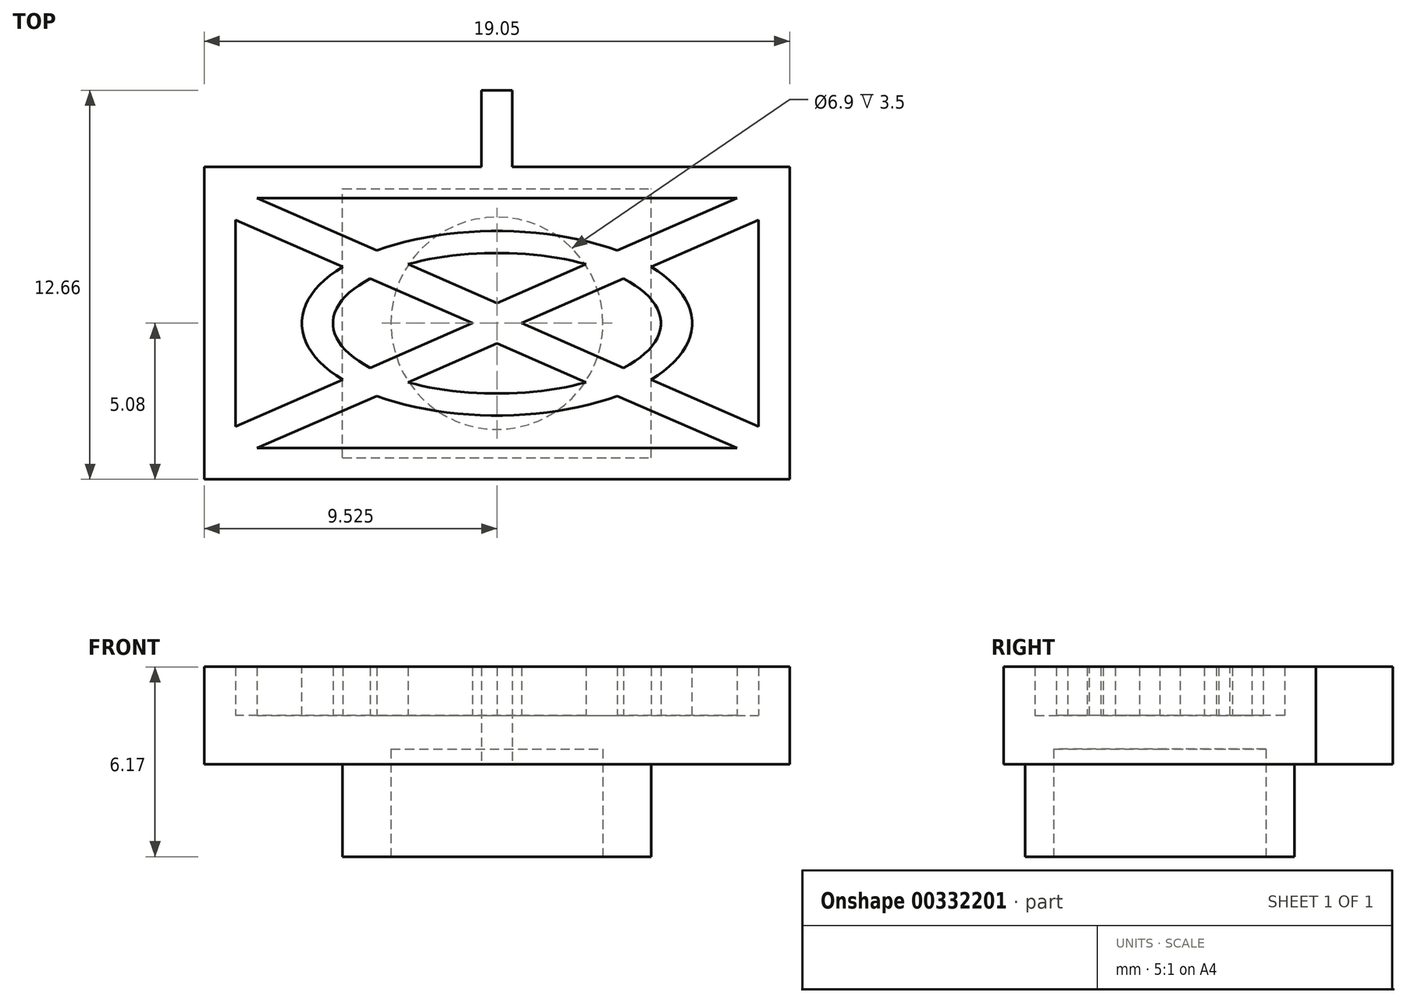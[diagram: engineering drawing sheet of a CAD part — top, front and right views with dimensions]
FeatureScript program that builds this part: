
annotation { "Feature Type Name" : "Feature", "Feature Type Description" : "" }
export const myFeature = defineFeature(function(context is Context, id is Id, definition is map)
    precondition{}
    {
        {
            var Q0;
            Q0=qCreatedBy(makeId("Top.planeOp"),FACE);
            var sketch = newSketch(context, id + "F0", { "sketchPlane" : qUnion([Q0])});
            skLineSegment(sketch, "E0.bottom", {"start": v(-19.05, 10.16) * mm, "end": v(0, 10.16) * mm});
            skLineSegment(sketch, "E0.top", {"start": v(-19.05, 0) * mm, "end": v(0, 0) * mm});
            skLineSegment(sketch, "E0.left", {"start": v(-19.05, 10.16) * mm, "end": v(-19.05, 0) * mm});
            skLineSegment(sketch, "E0.right", {"start": v(0, 10.16) * mm, "end": v(0, 0) * mm});
            skLineSegment(sketch, "E1", {"start": v(-9.52, 10.16) * mm, "end": v(-9.52, 0) * mm, "construction": true});
            skLineSegment(sketch, "E2.bottom", {"start": v(-10.02, 12.66) * mm, "end": v(-9.02, 12.66) * mm});
            skLineSegment(sketch, "E2.top", {"start": v(-10.02, 10.16) * mm, "end": v(-9.02, 10.16) * mm});
            skLineSegment(sketch, "E2.left", {"start": v(-10.02, 12.66) * mm, "end": v(-10.02, 10.16) * mm});
            skLineSegment(sketch, "E2.right", {"start": v(-9.02, 12.66) * mm, "end": v(-9.02, 10.16) * mm});
            skSolve(sketch);
        }
        {
            var Q0;
            Q0=qSketchRegion(id+"F0",true);
            extrude(context, id + "F1", {"entities" : qUnion([Q0]), "depth" : 3.17 * mm});
        }
        {
            var Q0;
            Q0=makeQuery(id+"F1.opExtrude","CAP_FACE",FACE,{"disambiguationData":[OSD([sQuery(id+"F0.wireOp",EDGE,"E0.bottom"),sQuery(id+"F0.wireOp",EDGE,"E0.top"),sQuery(id+"F0.wireOp",EDGE,"E0.left"),sQuery(id+"F0.wireOp",EDGE,"E0.right")])],"isStart":false});
            var sketch = newSketch(context, id + "F2", { "sketchPlane" : qUnion([Q0])});
            skLineSegment(sketch, "E3.bottom", {"start": v(-18.03, 9.14) * mm, "end": v(-1.02, 9.14) * mm});
            skLineSegment(sketch, "E3.top", {"start": v(-18.03, 1.02) * mm, "end": v(-1.02, 1.02) * mm});
            skLineSegment(sketch, "E3.left", {"start": v(-18.03, 9.14) * mm, "end": v(-18.03, 1.02) * mm});
            skLineSegment(sketch, "E3.right", {"start": v(-1.02, 9.14) * mm, "end": v(-1.02, 1.02) * mm});
            skSolve(sketch);
        }
        {
            var Q0;
            Q0=qSketchRegion(id+"F2",true);
            extrude(context, id + "F3", {"entities" : qUnion([Q0]), "operationType" : NewBodyOperationType.REMOVE, "oppositeDirection" : true, "depth" : 1.59 * mm});
        }
        {
            var Q0;
            {var subQ0=sQuery(id+"F2.wireOp",EDGE,"E3.bottom");var subQ1=sQuery(id+"F2.wireOp",EDGE,"E3.left");Q0=makeQuery(id+"FD6hazfNaiJcgqe_1.boolean.opBoolean","SPLIT",FACE,{"disambiguationData":[TD([makeQuery(id+"F3.boolean.opBoolean","COPY",FACE,{"derivedFrom":makeQuery(id+"F3.opExtrude","SWEPT_FACE",FACE,{"disambiguationData":[OSD([subQ0])]})})])],"derivedFrom":makeQuery(id+"F3.boolean.opBoolean","COPY",FACE,{"derivedFrom":makeQuery(id+"F3.opExtrude","CAP_FACE",FACE,{"disambiguationData":[OSD([subQ0,sQuery(id+"F2.wireOp",EDGE,"E3.top"),subQ1,sQuery(id+"F2.wireOp",EDGE,"E3.right")])],"isStart":false})})});}
            var sketch = newSketch(context, id + "F4", { "sketchPlane" : qUnion([Q0])});
            skLineSegment(sketch, "E4", {"start": v(-9.52, 10.16) * mm, "end": v(-9.52, 0) * mm, "construction": true});
            skLineSegment(sketch, "E5", {"start": v(-19.05, 5.08) * mm, "end": v(0, 5.08) * mm, "construction": true});
            skEllipse(sketch, "E6", {"center": v(-9.52, 5.08) * mm, "majorRadius": 5.33 * mm, "minorRadius": 2.29 * mm, "majorAxis": v(-1, 0)});
            skEllipse(sketch, "E7", {"center": v(-9.52, 5.08) * mm, "majorRadius": 6.35 * mm, "minorRadius": 3 * mm, "majorAxis": v(1, 0)});
            skSolve(sketch);
        }
        {
            var Q0;
            Q0=qSketchRegion(id+"F4",true);
            var Q1;
            Q1=makeQuery(id+"FD6hazfNaiJcgqe_1.boolean.opBoolean","MERGE",FACE,{"derivedFrom":[makeQuery(id+"F1.opExtrude","CAP_FACE",FACE,{"disambiguationData":[OSD([sQuery(id+"F0.wireOp",EDGE,"E0.bottom"),sQuery(id+"F0.wireOp",EDGE,"E0.top"),sQuery(id+"F0.wireOp",EDGE,"E0.left"),sQuery(id+"F0.wireOp",EDGE,"E0.right"),sQuery(id+"F0.wireOp",EDGE,"XctMcTzM-jzK6-gSmv-2nxO-Hmrl2WoydrkH.bottom"),sQuery(id+"F0.wireOp",EDGE,"XctMcTzM-jzK6-gSmv-2nxO-Hmrl2WoydrkH.left"),sQuery(id+"F0.wireOp",EDGE,"XctMcTzM-jzK6-gSmv-2nxO-Hmrl2WoydrkH.right")])],"isStart":false}),makeQuery(id+"FD6hazfNaiJcgqe_1.opExtrude","CAP_FACE",FACE,{"disambiguationData":[OSD([sQuery(id+"FBnKpMS2cNLFyNX_1.wireOp",EDGE,"OeS0QawB-iup7-bIXq-nBgO-fnigf9KOmNtt"),sQuery(id+"FBnKpMS2cNLFyNX_1.wireOp",EDGE,"xYslIAmR-IU4A-U8Ev-eRzx-1tLUXoU8zJ8x"),sQuery(id+"FBnKpMS2cNLFyNX_1.wireOp",EDGE,"s2yYm8nE-9nAX-yXiD-gElo-VwSO6LMNS3os"),sQuery(id+"FBnKpMS2cNLFyNX_1.wireOp",EDGE,"BWi2MzMB-bow1-vDxn-7ShQ-1YiDBgTSlN10"),sQuery(id+"FBnKpMS2cNLFyNX_1.wireOp",EDGE,"4fcJUz5v-7g5D-GTkM-eBk7-cmIldQICNH6a"),sQuery(id+"FBnKpMS2cNLFyNX_1.wireOp",EDGE,"JyWkrWma-j76y-q2y8-kGDN-Km0VDhZBhLyh"),sQuery(id+"FBnKpMS2cNLFyNX_1.wireOp",EDGE,"hH4EWFfC-tNwj-oGm0-8eoL-p1ctc8BhzRw8"),sQuery(id+"FBnKpMS2cNLFyNX_1.wireOp",EDGE,"unhDRoPr-LBfY-NyqK-AVhX-2gFjzCdnZd3x"),sQuery(id+"FBnKpMS2cNLFyNX_1.wireOp",EDGE,"eioCPEry-a7AL-AyuY-AUbQ-wWZvTsCijl4n"),sQuery(id+"FBnKpMS2cNLFyNX_1.wireOp",EDGE,"ga3sPcsW-uslI-afVP-5EuA-U3aNN3MUd2xP"),sQuery(id+"FBnKpMS2cNLFyNX_1.wireOp",EDGE,"2eZ3HgfS-F6HE-pDFD-BtrP-3SBC7ZAuQREh"),sQuery(id+"FBnKpMS2cNLFyNX_1.wireOp",EDGE,"egwDE0gL-gJxL-a5VO-DP01-p7e11LL6TNIh"),sQuery(id+"FBnKpMS2cNLFyNX_1.wireOp",EDGE,"Oc6yrfE5-Wmlw-YOVM-BoAX-kQYr9RLupFyV"),sQuery(id+"FBnKpMS2cNLFyNX_1.wireOp",EDGE,"HKjVjBGv-TE9a-NIGQ-HE8n-yFD3IG2zp62e")])],"isStart":false})]});
            extrude(context, id + "F5", {"entities" : qUnion([Q0]), "operationType" : NewBodyOperationType.ADD, "endBound" : BoundingType.UP_TO_SURFACE, "endBoundEntityFace" : qUnion([Q1]), "depth" : 25.4 * mm});
        }
        {
            var Q0;
            {var subQ1=sQuery(id+"F2.wireOp",EDGE,"E3.top");var subQ4=makeQuery(id+"F3.boolean.opBoolean","COPY",FACE,{"derivedFrom":makeQuery(id+"F3.opExtrude","SWEPT_FACE",FACE,{"disambiguationData":[OSD([subQ1])]})});var subQ6=sQuery(id+"F2.wireOp",EDGE,"E3.right");Q0=makeQuery(id+"F5.boolean.opBoolean","SPLIT",FACE,{"disambiguationData":[TD([subQ4])],"derivedFrom":makeQuery(id+"FD6hazfNaiJcgqe_1.boolean.opBoolean","SPLIT",FACE,{"disambiguationData":[TD([subQ4])],"derivedFrom":makeQuery(id+"F3.boolean.opBoolean","COPY",FACE,{"derivedFrom":makeQuery(id+"F3.opExtrude","CAP_FACE",FACE,{"disambiguationData":[OSD([sQuery(id+"F2.wireOp",EDGE,"E3.bottom"),subQ1,sQuery(id+"F2.wireOp",EDGE,"E3.left"),subQ6])],"isStart":false})})})});}
            var sketch = newSketch(context, id + "F6", { "sketchPlane" : qUnion([Q0])});
            skLineSegment(sketch, "E8", {"start": v(-19.05, 1.68) * mm, "end": v(-1.02, 1.68) * mm, "construction": true});
            skLineSegment(sketch, "E9", {"start": v(-9.53, 10.16) * mm, "end": v(-9.53, 0) * mm, "construction": true});
            skSolve(sketch);
        }
        {
            var Q0;
            Q0=makeQuery(id+"F1.opExtrude","CAP_FACE",FACE,{"disambiguationData":[OSD([sQuery(id+"F0.wireOp",EDGE,"E0.bottom"),sQuery(id+"F0.wireOp",EDGE,"E0.top"),sQuery(id+"F0.wireOp",EDGE,"E0.left"),sQuery(id+"F0.wireOp",EDGE,"E0.right"),sQuery(id+"F0.wireOp",EDGE,"iD4YVwzi-38ZZ-sZow-cuPB-LK5aPxXRs2tg"),sQuery(id+"F0.wireOp",EDGE,"25aa8db4-dd9b-41d2-b8c9-1594e9b75191"),sQuery(id+"F0.wireOp",EDGE,"40f63cb3-13d8-4821-a3c4-c05e674bd89b0.MirrorC")])],"isStart":true});
            var sketch = newSketch(context, id + "F7", { "sketchPlane" : qUnion([Q0])});
            skLineSegment(sketch, "E10.bottom", {"start": v(-14.55, -0.7) * mm, "end": v(-4.5, -0.7) * mm});
            skLineSegment(sketch, "E10.top", {"start": v(-14.55, -9.46) * mm, "end": v(-4.5, -9.46) * mm});
            skLineSegment(sketch, "E10.left", {"start": v(-14.55, -0.7) * mm, "end": v(-14.55, -9.46) * mm});
            skLineSegment(sketch, "E10.right", {"start": v(-4.5, -0.7) * mm, "end": v(-4.5, -9.46) * mm});
            skSolve(sketch);
        }
        {
            var Q0;
            Q0=qSketchRegion(id+"F7",true);
            extrude(context, id + "F8", {"entities" : qUnion([Q0]), "operationType" : NewBodyOperationType.ADD, "depth" : 3 * mm, "offsetDistance" : 25 * mm});
        }
        {
            var Q0;
            Q0=makeQuery(id+"F8.opExtrude","CAP_FACE",FACE,{"disambiguationData":[OSD([sQuery(id+"F7.wireOp",EDGE,"E10.bottom"),sQuery(id+"F7.wireOp",EDGE,"E10.top"),sQuery(id+"F7.wireOp",EDGE,"E10.left"),sQuery(id+"F7.wireOp",EDGE,"E10.right")])],"isStart":false});
            var sketch = newSketch(context, id + "F9", { "sketchPlane" : qUnion([Q0])});
            skCircle(sketch, "E11", {"center": v(-9.52, -5.08) * mm, "radius": 3.45 * mm});
            skLineSegment(sketch, "E12", {"start": v(-19.05, -5.08) * mm, "end": v(0, -5.08) * mm, "construction": true});
            skPoint(sketch, "E12.endSnap0", {"position": v(-4.5, -5.08) * mm});
            skLineSegment(sketch, "E13", {"start": v(-9.53, 0) * mm, "end": v(-9.53, -9.46) * mm, "construction": true});
            skSolve(sketch);
        }
        {
            var Q0;
            Q0=makeQuery(id+"F9.imprint","IMPRINT",FACE,{"disambiguationData":[TD([[makeQuery(id+"F9.imprint","IMPRINT",EDGE,{"derivedFrom":sQuery(id+"F9.wireOp",EDGE,"E11")}),1.0]])]});
            extrude(context, id + "F10", {"entities" : qUnion([Q0]), "operationType" : NewBodyOperationType.REMOVE, "oppositeDirection" : true, "depth" : 3.5 * mm, "offsetDistance" : 25 * mm});
        }
        {
            var Q0;
            Q0=makeQuery(id+"F6.imprint","IMPRINT",FACE,{"disambiguationData":[TD([[makeQuery(id+"F6.imprint","IMPRINT",EDGE,{"derivedFrom":makeQuery(id+"F3.boolean.opBoolean","COPY",EDGE,{"derivedFrom":makeQuery(id+"F3.opExtrude","CAP_EDGE",EDGE,{"disambiguationData":[OSD([sQuery(id+"F2.wireOp",EDGE,"E3.bottom")])],"isStart":false})})}),-1.0]])]});
            var sketch = newSketch(context, id + "F11", { "sketchPlane" : qUnion([Q0])});
            skLineSegment(sketch, "E14", {"start": v(-1.72, 9.14) * mm, "end": v(-9.53, 5.74) * mm});
            skLineSegment(sketch, "E15", {"start": v(-8.73, 5.08) * mm, "end": v(-1.02, 8.44) * mm});
            skLineSegment(sketch, "E16", {"start": v(-1.02, 8.44) * mm, "end": v(-1.02, 9.14) * mm});
            skLineSegment(sketch, "E17", {"start": v(-1.02, 9.14) * mm, "end": v(-1.72, 9.14) * mm});
            skLineSegment(sketch, "E18", {"start": v(-19.05, 5.08) * mm, "end": v(0, 5.08) * mm, "construction": true});
            skLineSegment(sketch, "E19.MirrorCS", {"start": v(-17.33, 9.14) * mm, "end": v(-9.53, 5.74) * mm});
            skLineSegment(sketch, "E20.MirrorCS", {"start": v(-10.33, 5.08) * mm, "end": v(-18.03, 8.44) * mm});
            skLineSegment(sketch, "E21.MirrorCS", {"start": v(-18.03, 8.44) * mm, "end": v(-18.03, 9.14) * mm});
            skLineSegment(sketch, "E22.MirrorCS", {"start": v(-18.03, 9.14) * mm, "end": v(-17.33, 9.14) * mm});
            skLineSegment(sketch, "E23.MirrorCS", {"start": v(-10.33, 5.08) * mm, "end": v(-18.03, 1.72) * mm});
            skLineSegment(sketch, "E24.MirrorCS", {"start": v(-8.73, 5.08) * mm, "end": v(-1.02, 1.72) * mm});
            skLineSegment(sketch, "E25.MirrorCS", {"start": v(-1.72, 1.02) * mm, "end": v(-9.53, 4.42) * mm});
            skLineSegment(sketch, "E26.MirrorCS", {"start": v(-17.33, 1.02) * mm, "end": v(-9.53, 4.42) * mm});
            skLineSegment(sketch, "E27.MirrorCS", {"start": v(-18.03, 1.02) * mm, "end": v(-17.33, 1.02) * mm});
            skLineSegment(sketch, "E28.MirrorCS", {"start": v(-18.03, 1.72) * mm, "end": v(-18.03, 1.02) * mm});
            skLineSegment(sketch, "E29.MirrorCS", {"start": v(-1.02, 1.72) * mm, "end": v(-1.02, 1.02) * mm});
            skLineSegment(sketch, "E30.MirrorCS", {"start": v(-1.02, 1.02) * mm, "end": v(-1.72, 1.02) * mm});
            skSolve(sketch);
        }
        {
            var Q0;
            Q0=qSketchRegion(id+"F11",true);
            var Q1;
            Q1=makeQuery(id+"FXsS83p9KQ4uv0L_1.boolean.opBoolean","MERGE",FACE,{"derivedFrom":[makeQuery(id+"F1.opExtrude","CAP_FACE",FACE,{"disambiguationData":[OSD([sQuery(id+"F0.wireOp",EDGE,"E0.bottom"),sQuery(id+"F0.wireOp",EDGE,"E0.top"),sQuery(id+"F0.wireOp",EDGE,"E0.left"),sQuery(id+"F0.wireOp",EDGE,"E0.right"),sQuery(id+"F0.wireOp",EDGE,"25aa8db4-dd9b-41d2-b8c9-1594e9b75191"),sQuery(id+"F0.wireOp",EDGE,"40f63cb3-13d8-4821-a3c4-c05e674bd89b0.MirrorC")])],"isStart":false}),makeQuery(id+"F5.opExtrude","CAP_FACE",FACE,{"disambiguationData":[OSD([sQuery(id+"F4.wireOp",EDGE,"E6"),sQuery(id+"F4.wireOp",EDGE,"E7")])],"isStart":false}),makeQuery(id+"FXsS83p9KQ4uv0L_1.opExtrude","CAP_FACE",FACE,{"disambiguationData":[OSD([sQuery(id+"Fi3yzKCDt9pSW51_1.wireOp",EDGE,"cutzoVbR-JFbv-1kZ0-SQrw-pSLFGMZcN76v"),sQuery(id+"Fi3yzKCDt9pSW51_1.wireOp",EDGE,"XYQyWRLz-35l4-wHee-0FsY-Oat0KQk3jhR6"),sQuery(id+"Fi3yzKCDt9pSW51_1.wireOp",EDGE,"lBgadLLx-aQS8-kMAZ-d5qN-Zo8duSUxtBeX"),sQuery(id+"Fi3yzKCDt9pSW51_1.wireOp",EDGE,"DlRPRQGx-Alaq-SPUL-URFH-jddu6C2Nnp9z"),sQuery(id+"Fi3yzKCDt9pSW51_1.wireOp",EDGE,"Shc4e2eY-gIsf-lYKj-D0sO-212MCfLGw1w2"),sQuery(id+"Fi3yzKCDt9pSW51_1.wireOp",EDGE,"DXv1RSob-CDWK-uPmN-nh2c-bdjhB3yjVnB2"),sQuery(id+"Fi3yzKCDt9pSW51_1.wireOp",EDGE,"Mjf90MPI-7UZW-OfA1-fD3l-TGEU1IJ1uaYu"),sQuery(id+"Fi3yzKCDt9pSW51_1.wireOp",EDGE,"IrneLFi4-a4Xm-RgwH-oJvY-WcCPALNDAReP"),sQuery(id+"Fi3yzKCDt9pSW51_1.wireOp",EDGE,"toQdHavX-h7D1-dxbV-IXrh-P84p4AImceJh"),sQuery(id+"Fi3yzKCDt9pSW51_1.wireOp",EDGE,"xGw8HYbu-oKFY-4S3u-lNNy-w4TfAhwJFqQu"),sQuery(id+"Fi3yzKCDt9pSW51_1.wireOp",EDGE,"5pvZd2gl-M8UA-9HNZ-daD7-4TEjzgTyMgsA"),sQuery(id+"Fi3yzKCDt9pSW51_1.wireOp",EDGE,"b1702624-0c59-4015-bc2e-a5f6b81265a70.MirrorCS"),sQuery(id+"Fi3yzKCDt9pSW51_1.wireOp",EDGE,"7deeccc9-7886-4666-b44c-47b900ed28990.MirrorCS"),sQuery(id+"Fi3yzKCDt9pSW51_1.wireOp",EDGE,"75936777-967d-44d6-aacf-753113c8b50b0.MirrorCS"),sQuery(id+"Fi3yzKCDt9pSW51_1.wireOp",EDGE,"e5875930-5b2f-47d0-b261-f87a419dd3ea0.MirrorCS"),sQuery(id+"Fi3yzKCDt9pSW51_1.wireOp",EDGE,"e1f8200d-9078-41b5-85b4-8a4adb8dc9e80.MirrorCS"),sQuery(id+"Fi3yzKCDt9pSW51_1.wireOp",EDGE,"40fd4d9e-f758-4b42-b7b5-3e08d0cf58f50.MirrorCS"),sQuery(id+"Fi3yzKCDt9pSW51_1.wireOp",EDGE,"553d3a6c-e9a7-4b40-b1d3-0817f640e5cc0.MirrorCS"),sQuery(id+"Fi3yzKCDt9pSW51_1.wireOp",EDGE,"5a723a2c-c48e-43ea-a32e-a11b15ff1a7b0.MirrorCS"),sQuery(id+"Fi3yzKCDt9pSW51_1.wireOp",EDGE,"932d58c0-4b54-410d-a467-0e9cf49887c90.MirrorCS"),sQuery(id+"Fi3yzKCDt9pSW51_1.wireOp",EDGE,"eeedfdb4-aa26-4e83-bf33-b18388155c4d0.MirrorCS"),sQuery(id+"Fi3yzKCDt9pSW51_1.wireOp",EDGE,"a4c71cba-da55-4cc9-80cf-8947727491d80.MirrorCS")])],"isStart":false})]});
            extrude(context, id + "F12", {"entities" : qUnion([Q0]), "operationType" : NewBodyOperationType.ADD, "endBound" : BoundingType.UP_TO_SURFACE, "depth" : 25 * mm, "endBoundEntityFace" : qUnion([Q1]), "offsetDistance" : 25 * mm});
        }
    });
